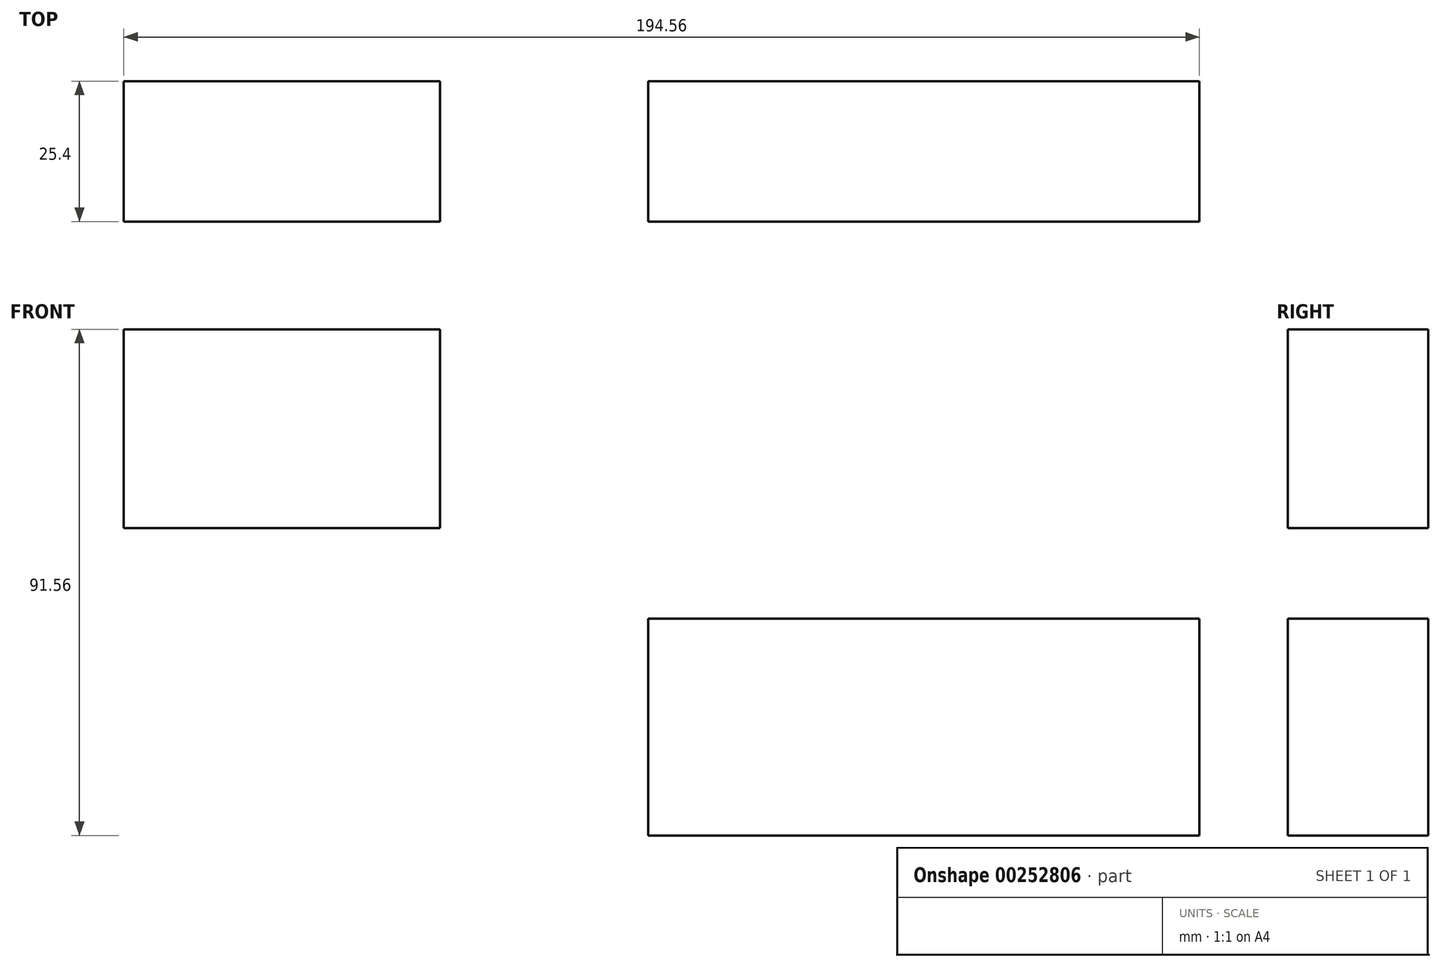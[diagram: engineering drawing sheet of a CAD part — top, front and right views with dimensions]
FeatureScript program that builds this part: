
annotation { "Feature Type Name" : "Feature", "Feature Type Description" : "" }
export const myFeature = defineFeature(function(context is Context, id is Id, definition is map)
    precondition{}
    {
        {
            var Q0;
            Q0=qCreatedBy(makeId("Front.planeOp"),FACE);
            var sketch = newSketch(context, id + "F0", { "sketchPlane" : qUnion([Q0])});
            skLineSegment(sketch, "E0.bottom", {"start": v(49.66, -19.21) * mm, "end": v(-50.07, -19.21) * mm});
            skLineSegment(sketch, "E0.top", {"start": v(49.66, 20.03) * mm, "end": v(-50.07, 20.03) * mm});
            skLineSegment(sketch, "E0.left", {"start": v(49.66, -19.21) * mm, "end": v(49.66, 20.03) * mm});
            skLineSegment(sketch, "E0.right", {"start": v(-50.07, -19.21) * mm, "end": v(-50.07, 20.03) * mm});
            skPoint(sketch, "E0.middle", {"position": v(-0.2, 0.4) * mm});
            skLineSegment(sketch, "E1.bottom", {"start": v(-87.68, 36.38) * mm, "end": v(-144.9, 36.38) * mm});
            skLineSegment(sketch, "E1.top", {"start": v(-87.68, 72.35) * mm, "end": v(-144.9, 72.35) * mm});
            skLineSegment(sketch, "E1.left", {"start": v(-87.68, 36.38) * mm, "end": v(-87.68, 72.35) * mm});
            skLineSegment(sketch, "E1.right", {"start": v(-144.9, 36.38) * mm, "end": v(-144.9, 72.35) * mm});
            skPoint(sketch, "E1.middle", {"position": v(-116.3, 54.36) * mm});
            skLineSegment(sketch, "E2", {"start": v(-50.07, 4.09) * mm, "end": v(-50.07, 20.03) * mm});
            skSolve(sketch);
        }
        {
            var Q0;
            Q0=makeQuery(id+"F0.imprint","IMPRINT",FACE,{"disambiguationData":[TD([[makeQuery(id+"F0.imprint","IMPRINT",EDGE,{"derivedFrom":sQuery(id+"F0.wireOp",EDGE,"E1.bottom")}),-1.0]])]});
            extrude(context, id + "F1", {"entities" : qUnion([Q0]), "depth" : 25.4 * mm});
        }
        {
            var Q0;
            Q0=qSketchRegion(id+"F0",true);
            extrude(context, id + "F2", {"entities" : qUnion([Q0]), "operationType" : NewBodyOperationType.ADD, "depth" : 25.4 * mm});
        }
    });
